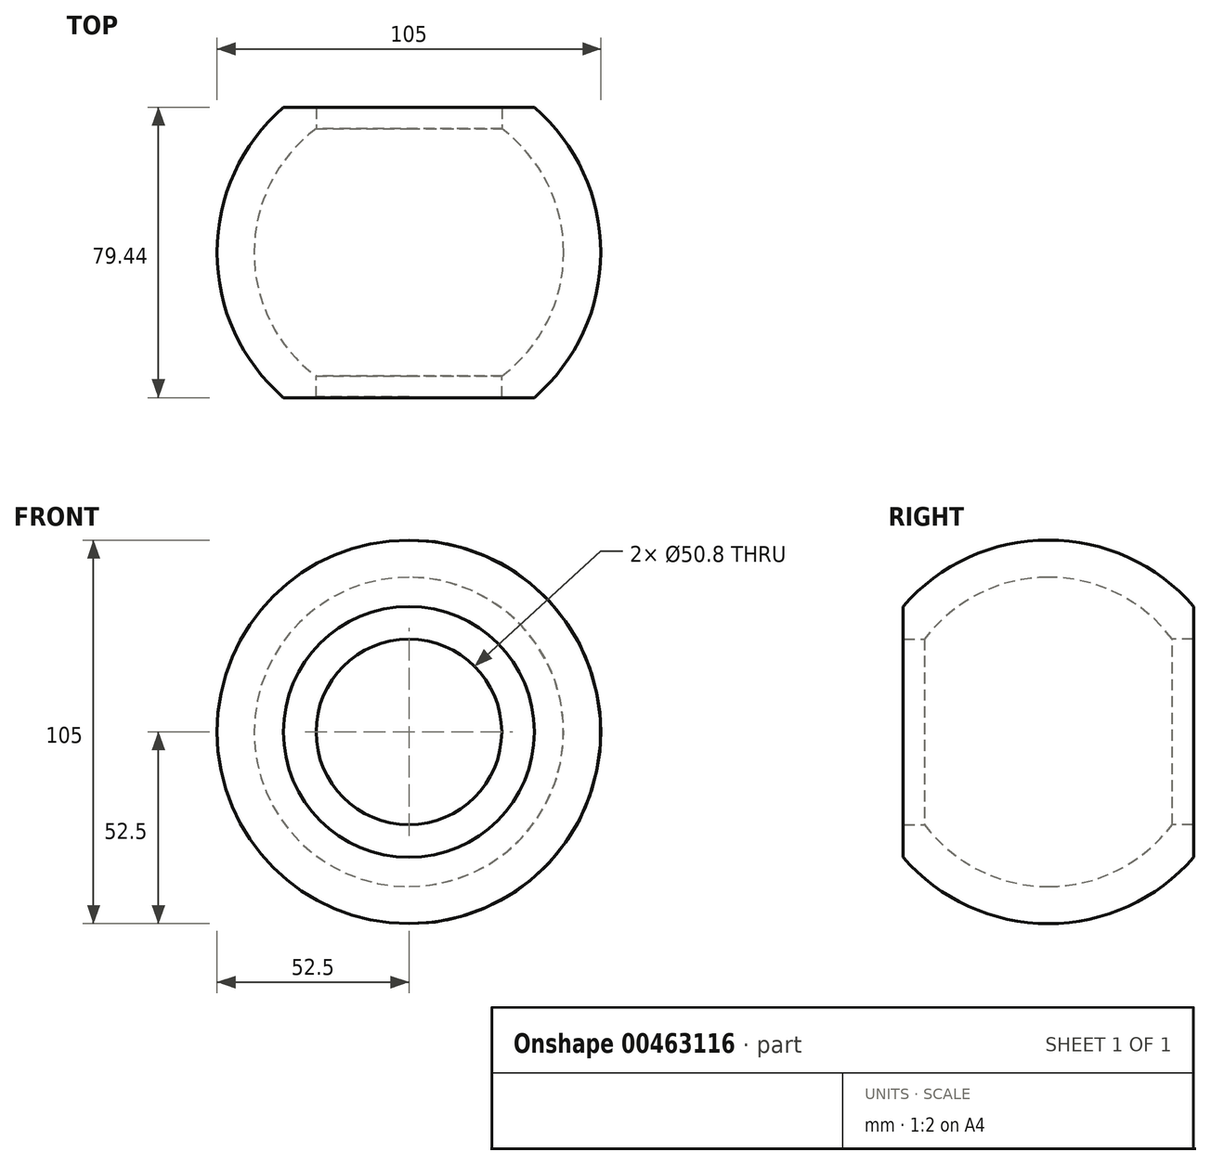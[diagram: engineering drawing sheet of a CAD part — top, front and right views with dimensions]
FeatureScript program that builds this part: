
annotation { "Feature Type Name" : "Feature", "Feature Type Description" : "" }
export const myFeature = defineFeature(function(context is Context, id is Id, definition is map)
    precondition{}
    {
        {
            var Q0;
            Q0=qCreatedBy(makeId("Front.planeOp"),FACE);
            var sketch = newSketch(context, id + "F0", { "sketchPlane" : qUnion([Q0])});
            skCircle(sketch, "E0", {"center": v(0, 0) * mm, "radius": 52.5 * mm});
            skLineSegment(sketch, "E1", {"start": v(0, 69.8) * mm, "end": v(0, -74.03) * mm});
            skPoint(sketch, "E2", {"position": v(0, 52.5) * mm});
            skSolve(sketch);
        }
        {
            var Q0;
            {var subQ0=sQuery(id+"F0.wireOp",EDGE,"E1");var subQ1=sQuery(id+"F0.wireOp",EDGE,"E0");var subQ2=makeQuery(id+"F0.imprint","INTERSECT",VERTEX,{"disambiguationData":[OD(0.0)],"derivedFrom":[subQ1,subQ0]});Q0=makeQuery(id+"F0.imprint","IMPRINT",FACE,{"disambiguationData":[TD([[makeQuery(id+"F0.imprint","IMPRINT",EDGE,{"disambiguationData":[TD([[subQ2,1.0]])],"derivedFrom":subQ1}),1.0]])]});}
            var Q1;
            Q1=sQuery(id+"F0.wireOp",EDGE,"E1");
            revolve(context, id + "F1", {"entities" : qUnion([Q0]), "axis" : qUnion([Q1]), "revolveType" : RevolveType.ONE_DIRECTION, "angle" : 180 * degree});
        }
        {
            var Q0;
            Q0=makeQuery(id+"F1.opRevolve","SWEPT_BODY",BODY,{"disambiguationData":[OSD([sQuery(id+"F0.wireOp",EDGE,"E0"),sQuery(id+"F0.wireOp",EDGE,"E1")])]});
            var Q1;
            Q1=makeQuery(id+"F1.opRevolve","CAP_FACE",FACE,{"disambiguationData":[OSD([sQuery(id+"F0.wireOp",EDGE,"E0"),sQuery(id+"F0.wireOp",EDGE,"E1")])],"isStart":false});
            mirror(context, id + "F2", {"operationType" : NewBodyOperationType.ADD, "entities" : qUnion([Q0]), "mirrorPlane" : qUnion([Q1])});
        }
        {
            var Q0;
            {var subQ0=makeQuery(id+"F1.opRevolve","SWEPT_FACE",FACE,{"disambiguationData":[OSD([sQuery(id+"F0.wireOp",EDGE,"E0")])]});Q0=makeQuery(id+"F2.boolean.opBoolean","MERGE",FACE,{"derivedFrom":[subQ0,makeQuery(id+"F2.opPattern","COPY",FACE,{"derivedFrom":subQ0,"instanceName":"1"})]});}
            var Q1;
            Q1=makeQuery(id+"F1.opRevolve","SWEPT_BODY",BODY,{"disambiguationData":[OSD([sQuery(id+"F0.wireOp",EDGE,"E0"),sQuery(id+"F0.wireOp",EDGE,"E1")])]});
            shell(context, id + "F3", {"isHollow" : true, "entities" : qUnion([Q0]), "parts" : qUnion([Q1]), "thickness" : 10.16 * mm});
        }
        {
            var Q0;
            Q0=sQuery(id+"F0.wireOp",VERTEX,"E0.center");
            var Q1;
            Q1=makeQuery(id+"F1.opRevolve","SWEPT_BODY",BODY,{"disambiguationData":[OSD([sQuery(id+"F0.wireOp",EDGE,"E0"),sQuery(id+"F0.wireOp",EDGE,"E1")])]});
            hole(context, id + "F4", {"style" : HoleStyle.SIMPLE, "endStyle" : HoleEndStyle.THROUGH, "holeDiameter" : 50.8 * mm, "isTappedThrough" : true, "tappedDepth" : 12.7 * mm, "tapClearance" : 3, "startFromSketch" : true, "locations" : qUnion([Q0]), "scope" : qUnion([Q1])});
        }
        {
            var Q0;
            Q0=sQuery(id+"F0.wireOp",VERTEX,"E0.center");
            var Q1;
            Q1=makeQuery(id+"F1.opRevolve","SWEPT_BODY",BODY,{"disambiguationData":[OSD([sQuery(id+"F0.wireOp",EDGE,"E0"),sQuery(id+"F0.wireOp",EDGE,"E1")])]});
            hole(context, id + "F5", {"style" : HoleStyle.SIMPLE, "endStyle" : HoleEndStyle.THROUGH, "oppositeDirection" : true, "holeDiameter" : 50.8 * mm, "isTappedThrough" : true, "tappedDepth" : 12.7 * mm, "tapClearance" : 3, "locations" : qUnion([Q0]), "scope" : qUnion([Q1])});
        }
        {
            var Q0;
            {var subQ0=makeQuery(id+"F1.opRevolve","SWEPT_FACE",FACE,{"disambiguationData":[OSD([sQuery(id+"F0.wireOp",EDGE,"E0")])]});Q0=makeQuery(id+"F5.hole-0.boolean.opBoolean","INTERSECT",EDGE,{"derivedFrom":[makeQuery(id+"F2.boolean.opBoolean","MERGE",FACE,{"derivedFrom":[subQ0,makeQuery(id+"F2.opPattern","COPY",FACE,{"derivedFrom":subQ0,"instanceName":"1"})]}),makeQuery(id+"F5.hole-0.opRevolve","SWEPT_FACE",FACE,{"disambiguationData":[OSD([sQuery(id+"F5.hole-0.sketch.wireOp",EDGE,"core_line_2")])]})]});}
            var Q1;
            {var subQ0=makeQuery(id+"F1.opRevolve","SWEPT_FACE",FACE,{"disambiguationData":[OSD([sQuery(id+"F0.wireOp",EDGE,"E0")])]});Q1=makeQuery(id+"F4.hole-0.boolean.opBoolean","INTERSECT",EDGE,{"derivedFrom":[makeQuery(id+"F2.boolean.opBoolean","MERGE",FACE,{"derivedFrom":[subQ0,makeQuery(id+"F2.opPattern","COPY",FACE,{"derivedFrom":subQ0,"instanceName":"1"})]}),makeQuery(id+"F4.hole-0.opRevolve","SWEPT_FACE",FACE,{"disambiguationData":[OSD([sQuery(id+"F4.hole-0.sketch.wireOp",EDGE,"core_line_2")])]})]});}
            var Q2;
            {var subQ0=makeQuery(id+"F1.opRevolve","SWEPT_FACE",FACE,{"disambiguationData":[OSD([sQuery(id+"F0.wireOp",EDGE,"E0")])]});Q2=makeQuery(id+"F2.boolean.opBoolean","MERGE",FACE,{"derivedFrom":[subQ0,makeQuery(id+"F2.opPattern","COPY",FACE,{"derivedFrom":subQ0,"instanceName":"1"})]});}
            chamfer(context, id + "F6", {"entities" : qUnion([Q0, Q1, Q2]), "chamferType" : ChamferType.OFFSET_ANGLE, "width" : 10.16 * mm, "oppositeDirection" : false, "angle" : 30 * degree, "tangentPropagation" : true});
        }
    });
